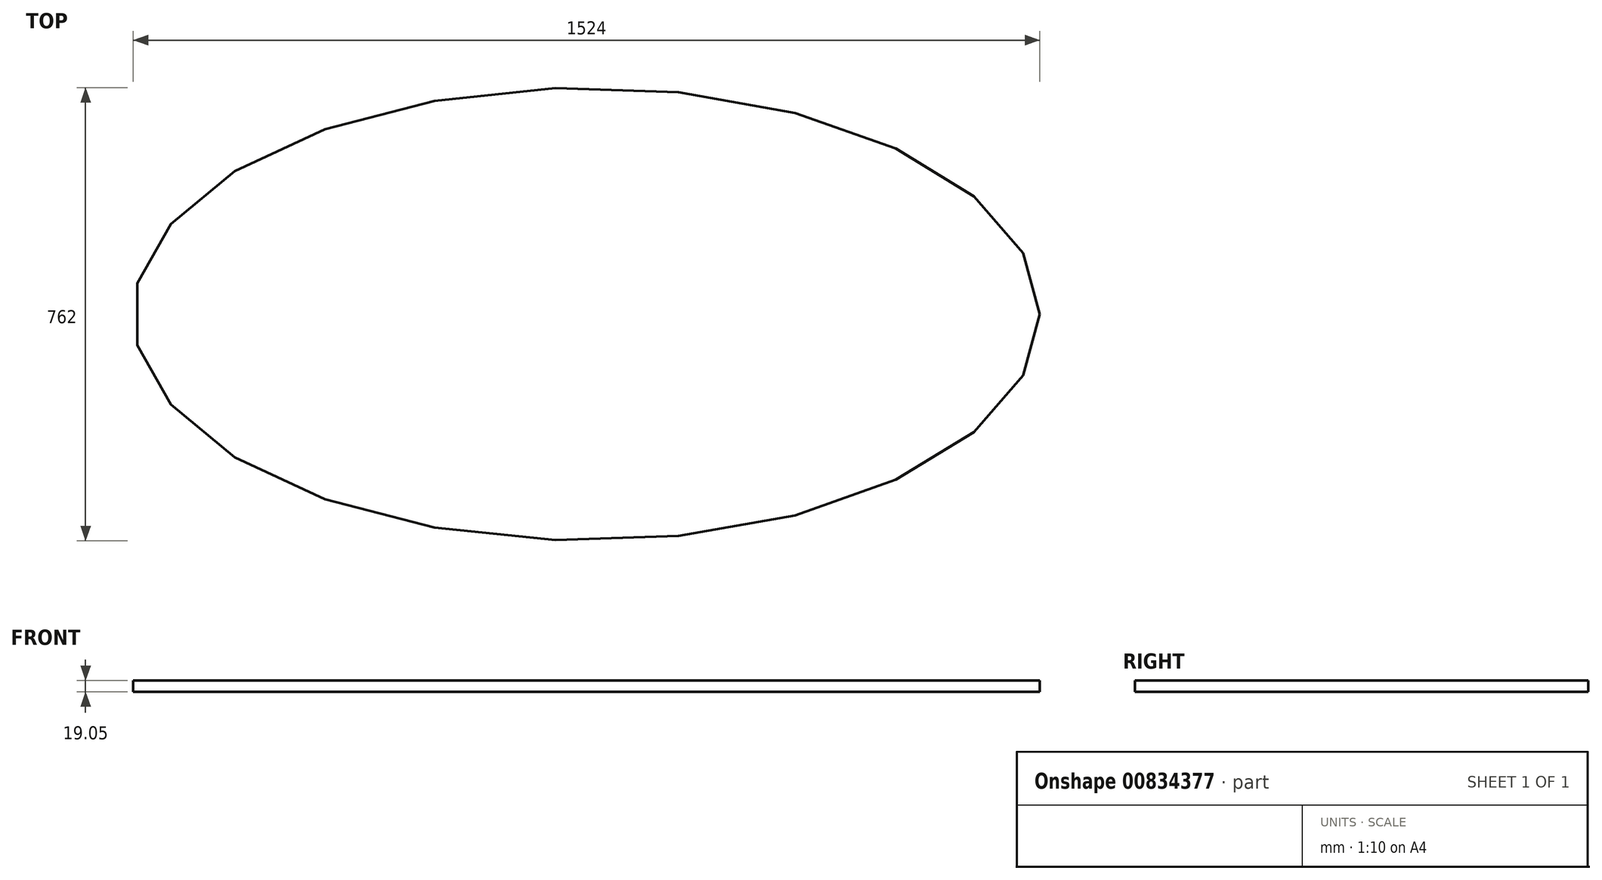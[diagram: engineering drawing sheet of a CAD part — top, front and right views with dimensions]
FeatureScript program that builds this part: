
annotation { "Feature Type Name" : "Feature", "Feature Type Description" : "" }
export const myFeature = defineFeature(function(context is Context, id is Id, definition is map)
    precondition{}
    {
        {
            var Q0;
            Q0=qCreatedBy(makeId("Top.planeOp"),FACE);
            var sketch = newSketch(context, id + "F0", { "sketchPlane" : qUnion([Q0])});
            skEllipse(sketch, "E0", {"center": v(0, 0) * mm, "majorRadius": 762 * mm, "minorRadius": 381 * mm, "majorAxis": v(1, 0)});
            skSolve(sketch);
        }
        {
            var Q0;
            Q0 = qSketchRegion(id + "F0", true);
            extrude(context, id + "F1", {"entities" : qUnion([Q0]), "depth" : 19.05 * mm, "offsetDistance" : 25.4 * mm});
        }
    });
